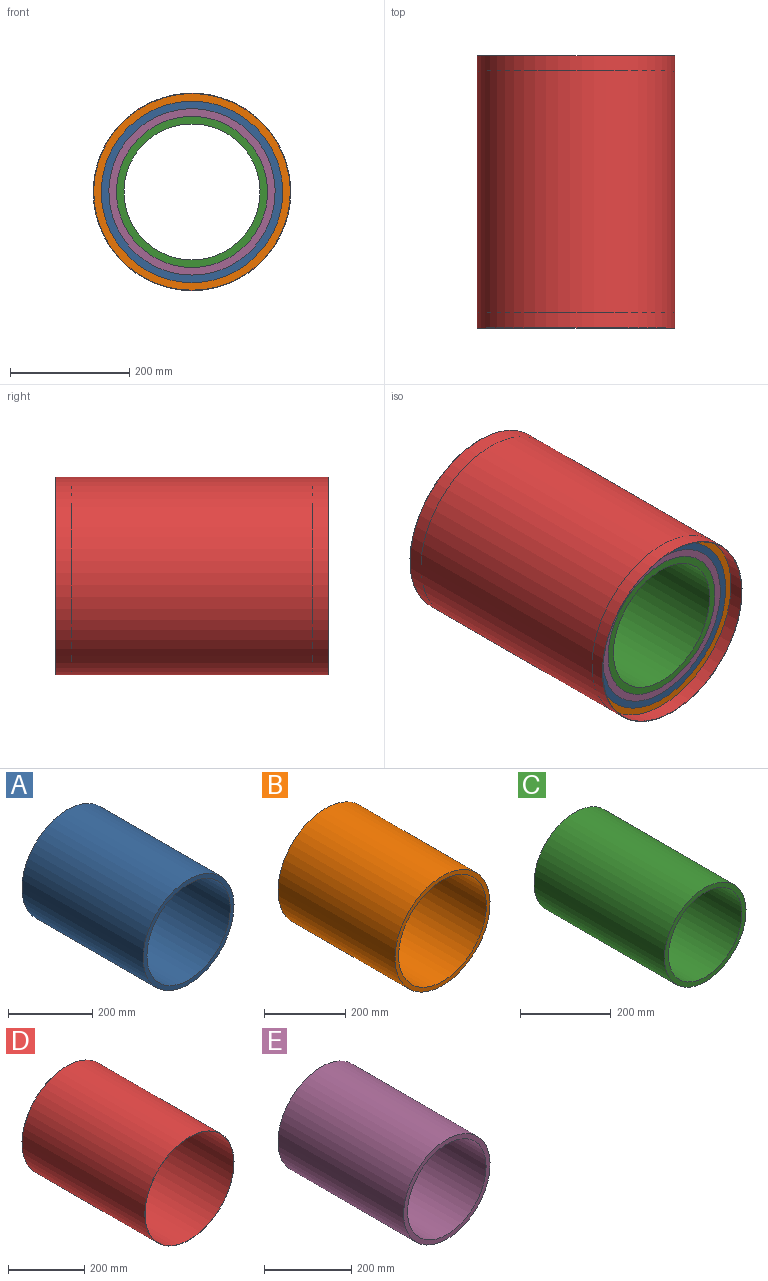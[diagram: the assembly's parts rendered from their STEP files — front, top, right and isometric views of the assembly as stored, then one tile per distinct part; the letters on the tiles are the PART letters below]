
ASSEMBLY  parts=5 mates=8
PART A: 4 faces, bbox 304.8x406.4x304.8 mm
  f0: cylinder r=139.7mm len=406.4mm, axis (0,1,0), area 356722.1mm2, adj f2,f3
  f1: cylinder r=152.4mm len=406.4mm, axis (0,1,0), area 389151.3mm2, adj f2,f3
  f2: plane 304.8x304.8mm, normal (0,-1,0), area 11654.3mm2, adj f0,f1
  f3: plane 304.8x304.8mm, normal (0,1,0), area 11654.3mm2, adj f0,f1
PART B: 4 faces, bbox 330.2x406.4x330.2 mm
  f0: cylinder r=152.4mm len=406.4mm, axis (0,1,0), area 389151.3mm2, adj f2,f3
  f1: cylinder r=165.1mm len=406.4mm, axis (0,1,0), area 421580.6mm2, adj f2,f3
  f2: plane 330.2x330.2mm, normal (0,-1,0), area 12667.7mm2, adj f0,f1
  f3: plane 330.2x330.2mm, normal (0,1,0), area 12667.7mm2, adj f0,f1
PART C: 4 faces, bbox 254x406.4x254 mm
  f0: cylinder r=114.3mm len=406.4mm, axis (0,1,0), area 291863.5mm2, adj f2,f3
  f1: cylinder r=127mm len=406.4mm, axis (0,1,0), area 324292.8mm2, adj f2,f3
  f2: plane 254x254mm, normal (0,-1,0), area 9627.4mm2, adj f0,f1
  f3: plane 254x254mm, normal (0,1,0), area 9627.4mm2, adj f0,f1
PART D: 4 faces, bbox 331.8x457.2x331.8 mm
  f0: cylinder r=165.1mm len=457.2mm, axis (0,1,0), area 474278.2mm2, adj f2,f3
  f1: cylinder r=165.89mm len=457.2mm, axis (0,1,0), area 476558.4mm2, adj f2,f3
  f2: plane 331.79x331.79mm, normal (0,-1,0), area 825.4mm2, adj f0,f1
  f3: plane 331.79x331.79mm, normal (0,1,0), area 825.4mm2, adj f0,f1
PART E: 4 faces, bbox 279.4x406.4x279.4 mm
  f0: cylinder r=127mm len=406.4mm, axis (0,1,0), area 324292.8mm2, adj f2,f3
  f1: cylinder r=139.7mm len=406.4mm, axis (0,1,0), area 356722.1mm2, adj f2,f3
  f2: plane 279.4x279.4mm, normal (0,-1,0), area 10640.9mm2, adj f0,f1
  f3: plane 279.4x279.4mm, normal (0,1,0), area 10640.9mm2, adj f0,f1
PLACE A t=(557.66,416.84,638.92)mm
PLACE B t=(-661.54,416.84,638.92)mm
PLACE C t=(557.66,416.84,-580.28)mm
PLACE D t=(-51.94,442.24,29.32)mm
PLACE E t=(-661.54,416.84,-580.28)mm
MATE planar E.f0 <-> C.f0  axis (0,-1,0) through (-51.94,10.44,29.32)mm
MATE planar D.f1 <-> A.f0  axis (0,-1,0) through (-51.94,-14.96,29.32)mm
MATE cylindrical A.f0 <-> B.f0  axis (0,-1,0) through (-51.94,10.44,29.32)mm
MATE planar A.f0 <-> E.f0  axis (0,-1,0) through (-51.94,10.44,29.32)mm
MATE cylindrical C.f0 <-> E.f0  axis (0,-1,0) through (-51.94,10.44,29.32)mm
MATE planar B.f0 <-> A.f0  axis (0,1,0) through (-51.94,416.84,29.32)mm
MATE cylindrical B.f0 <-> D.f0  axis (0,-1,0) through (-51.94,10.44,29.32)mm
MATE cylindrical E.f0 <-> A.f0  axis (0,-1,0) through (-51.94,10.44,29.32)mm
